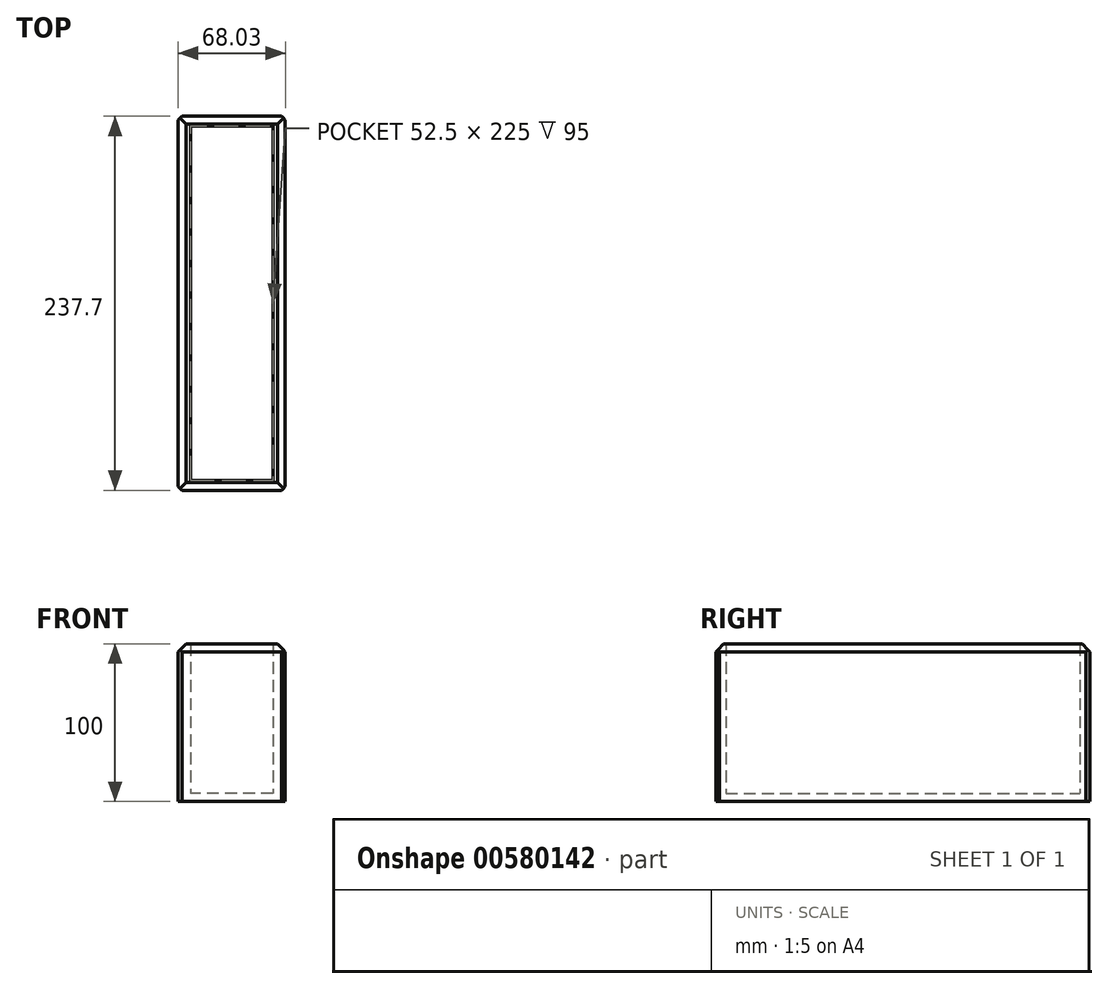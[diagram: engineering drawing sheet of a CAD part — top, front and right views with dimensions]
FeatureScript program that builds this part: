
annotation { "Feature Type Name" : "Feature", "Feature Type Description" : "" }
export const myFeature = defineFeature(function(context is Context, id is Id, definition is map)
    precondition{}
    {
        {
            var Q0;
            Q0=qCreatedBy(makeId("Top.planeOp"),FACE);
            var sketch = newSketch(context, id + "F0", { "sketchPlane" : qUnion([Q0])});
            skLineSegment(sketch, "E0.bottom", {"start": v(-48.3, 112.5) * mm, "end": v(4.2, 112.5) * mm});
            skLineSegment(sketch, "E0.top", {"start": v(-48.3, -112.5) * mm, "end": v(4.2, -112.5) * mm});
            skLineSegment(sketch, "E0.left", {"start": v(-48.3, 112.5) * mm, "end": v(-48.3, -112.5) * mm});
            skLineSegment(sketch, "E0.right", {"start": v(4.2, 112.5) * mm, "end": v(4.2, -112.5) * mm});
            skLineSegment(sketch, "E1.bottom", {"start": v(11.97, 118.85) * mm, "end": v(-56.06, 118.85) * mm});
            skLineSegment(sketch, "E1.top", {"start": v(11.97, -118.85) * mm, "end": v(-56.06, -118.85) * mm});
            skLineSegment(sketch, "E1.left", {"start": v(11.97, 118.85) * mm, "end": v(11.97, -118.85) * mm});
            skLineSegment(sketch, "E1.right", {"start": v(-56.06, 118.85) * mm, "end": v(-56.06, -118.85) * mm});
            skPoint(sketch, "E1.middle", {"position": v(-22.05, 0) * mm});
            skPoint(sketch, "E1.middle.positionSnap0", {"position": v(-22.05, 112.5) * mm});
            skPoint(sketch, "E1.middle.positionSnap1", {"position": v(-48.3, 0) * mm});
            skPoint(sketch, "E1.centerSnap0", {"position": v(-22.05, 112.5) * mm});
            skPoint(sketch, "E1.centerSnap1", {"position": v(-48.3, 0) * mm});
            skSolve(sketch);
        }
        {
            var Q0;
            Q0=makeQuery(id+"F0.imprint","IMPRINT",FACE,{"disambiguationData":[TD([[makeQuery(id+"F0.imprint","IMPRINT",EDGE,{"derivedFrom":sQuery(id+"F0.wireOp",EDGE,"E0.bottom")}),1.0]])]});
            extrude(context, id + "F1", {"entities" : qUnion([Q0]), "depth" : 100 * mm, "offsetDistance" : 25 * mm});
        }
        {
            var Q0;
            Q0=makeQuery(id+"F1.opExtrude","SWEPT_FACE",FACE,{"disambiguationData":[OSD([sQuery(id+"F0.wireOp",EDGE,"E0.left")])]});
            var sketch = newSketch(context, id + "F2", { "sketchPlane" : qUnion([Q0])});
            skLineSegment(sketch, "E2.bottom", {"start": v(-112.5, 0) * mm, "end": v(112.5, 0) * mm});
            skLineSegment(sketch, "E2.top", {"start": v(-112.5, 5) * mm, "end": v(112.5, 5) * mm});
            skLineSegment(sketch, "E2.left", {"start": v(-112.5, 0) * mm, "end": v(-112.5, 5) * mm});
            skLineSegment(sketch, "E2.right", {"start": v(112.5, 0) * mm, "end": v(112.5, 5) * mm});
            skSolve(sketch);
        }
        {
            var Q0;
            Q0 = qSketchRegion(id + "F2", true);
            extrude(context, id + "F3", {"entities" : qUnion([Q0]), "operationType" : NewBodyOperationType.ADD, "depth" : 52.5 * mm, "offsetDistance" : 25 * mm});
        }
        {
            var Q0;
            Q0=makeQuery(id+"F1.opExtrude","CAP_EDGE",EDGE,{"disambiguationData":[OSD([sQuery(id+"F0.wireOp",EDGE,"E1.right")])],"isStart":false});
            var Q1;
            Q1=makeQuery(id+"F1.opExtrude","CAP_EDGE",EDGE,{"disambiguationData":[OSD([sQuery(id+"F0.wireOp",EDGE,"E1.top")])],"isStart":false});
            var Q2;
            Q2=makeQuery(id+"F1.opExtrude","CAP_EDGE",EDGE,{"disambiguationData":[OSD([sQuery(id+"F0.wireOp",EDGE,"E1.left")])],"isStart":false});
            var Q3;
            Q3=makeQuery(id+"F1.opExtrude","CAP_EDGE",EDGE,{"disambiguationData":[OSD([sQuery(id+"F0.wireOp",EDGE,"E1.bottom")])],"isStart":false});
            chamfer(context, id + "F4", {"entities" : qUnion([Q0, Q1, Q2, Q3]), "width" : 5 * mm, "tangentPropagation" : true});
        }
        {
            var Q0;
            Q0=makeQuery(id+"F1.opExtrude","SWEPT_EDGE",EDGE,{"disambiguationData":[OSD([sQuery(id+"F0.wireOp",EDGE,"E1.top"),sQuery(id+"F0.wireOp",EDGE,"E1.right")])]});
            var Q1;
            Q1=makeQuery(id+"F1.opExtrude","SWEPT_EDGE",EDGE,{"disambiguationData":[OSD([sQuery(id+"F0.wireOp",EDGE,"E1.top"),sQuery(id+"F0.wireOp",EDGE,"E1.left")])]});
            var Q2;
            Q2=makeQuery(id+"F1.opExtrude","SWEPT_EDGE",EDGE,{"disambiguationData":[OSD([sQuery(id+"F0.wireOp",EDGE,"E1.bottom"),sQuery(id+"F0.wireOp",EDGE,"E1.left")])]});
            var Q3;
            Q3=makeQuery(id+"F1.opExtrude","SWEPT_EDGE",EDGE,{"disambiguationData":[OSD([sQuery(id+"F0.wireOp",EDGE,"E1.bottom"),sQuery(id+"F0.wireOp",EDGE,"E1.right")])]});
            chamfer(context, id + "F5", {"entities" : qUnion([Q0, Q1, Q2, Q3]), "width" : 2.5 * mm, "tangentPropagation" : true});
        }
    });
